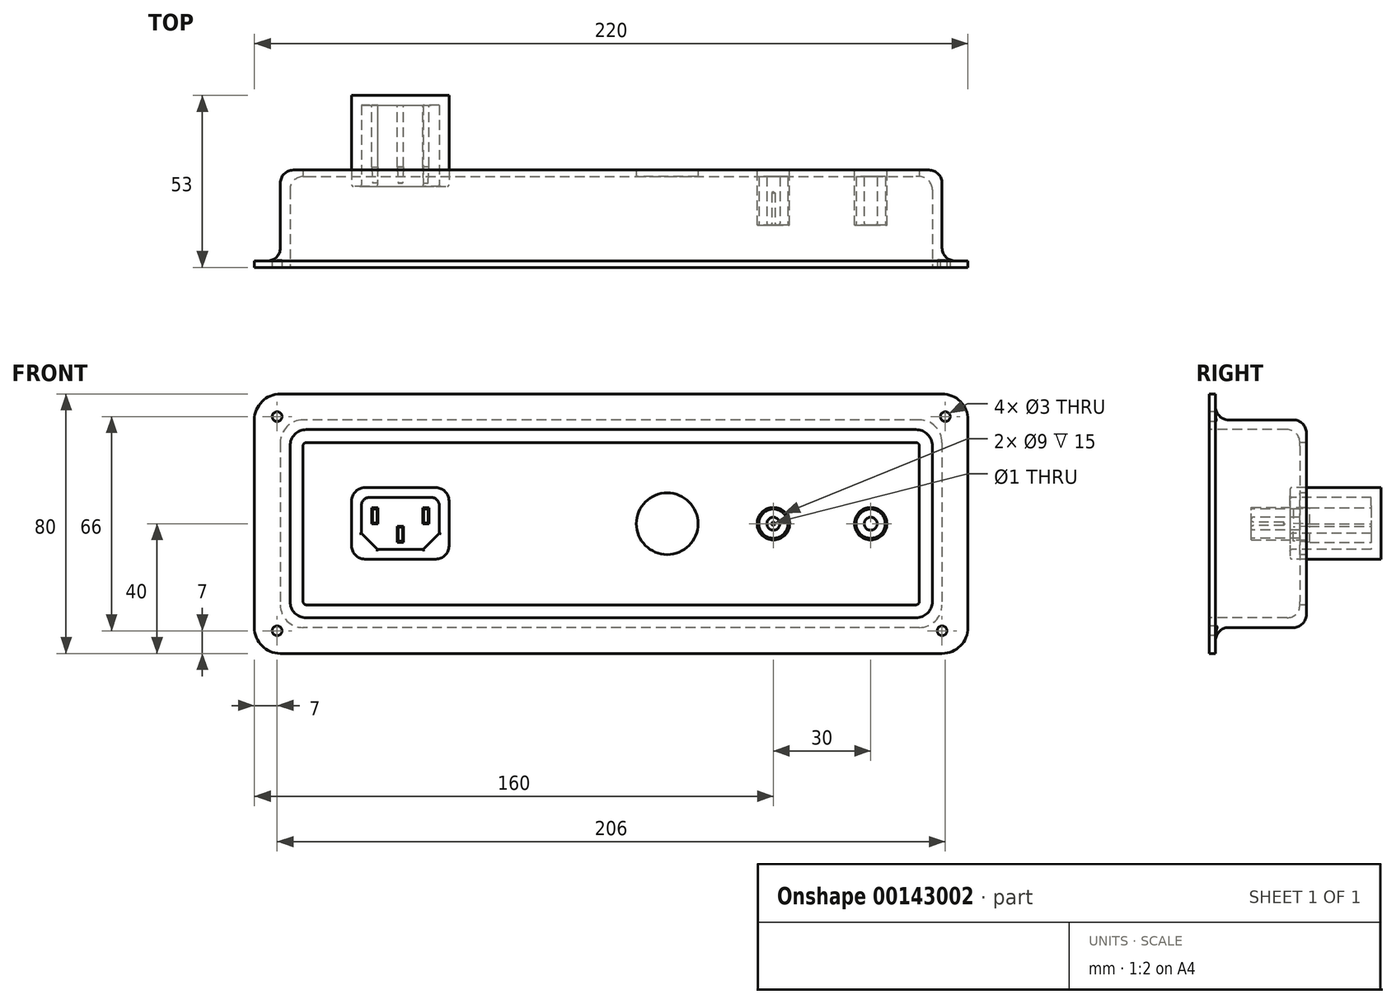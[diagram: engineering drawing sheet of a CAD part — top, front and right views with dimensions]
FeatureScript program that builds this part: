
annotation { "Feature Type Name" : "Feature", "Feature Type Description" : "" }
export const myFeature = defineFeature(function(context is Context, id is Id, definition is map)
    precondition{}
    {
        {
            var Q0;
            Q0=qCreatedBy(makeId("Front.planeOp"),FACE);
            var sketch = newSketch(context, id + "F0", { "sketchPlane" : qUnion([Q0])});
            skLineSegment(sketch, "E0.bottom", {"start": v(8, 0) * mm, "end": v(212, 0) * mm});
            skLineSegment(sketch, "E0.top", {"start": v(8, 80) * mm, "end": v(212, 80) * mm});
            skLineSegment(sketch, "E0.left", {"start": v(0, 8) * mm, "end": v(0, 72) * mm});
            skLineSegment(sketch, "E0.right", {"start": v(220, 8) * mm, "end": v(220, 72) * mm});
            skPoint(sketch, "E1.visualSharp", {"position": v(0, 80) * mm});
            skArc(sketch, "E1.filletArc", {"start": v(8, 80) * mm, "mid": v(2.34, 77.66) * mm, "end": v(0, 72) * mm});
            skPoint(sketch, "E2.visualSharp", {"position": v(220, 80) * mm});
            skArc(sketch, "E2.filletArc", {"start": v(220, 72) * mm, "mid": v(217.66, 77.66) * mm, "end": v(212, 80) * mm});
            skPoint(sketch, "E3.visualSharp", {"position": v(0, 0) * mm});
            skArc(sketch, "E3.filletArc", {"start": v(0, 8) * mm, "mid": v(2.34, 2.34) * mm, "end": v(8, 0) * mm});
            skPoint(sketch, "E4.visualSharp", {"position": v(220, 0) * mm});
            skArc(sketch, "E4.filletArc", {"start": v(212, 0) * mm, "mid": v(217.66, 2.34) * mm, "end": v(220, 8) * mm});
            skSolve(sketch);
        }
        {
            var Q0;
            Q0 = qSketchRegion(id + "F0", true);
            extrude(context, id + "F1", {"entities" : qUnion([Q0]), "depth" : 30 * mm});
        }
        {
            var Q0;
            Q0=makeQuery(id+"F1.opExtrude","CAP_FACE",FACE,{"disambiguationData":[OSD([sQuery(id+"F0.wireOp",EDGE,"E0.bottom"),sQuery(id+"F0.wireOp",EDGE,"E0.top"),sQuery(id+"F0.wireOp",EDGE,"E0.left"),sQuery(id+"F0.wireOp",EDGE,"E0.right"),sQuery(id+"F0.wireOp",EDGE,"E1.filletArc"),sQuery(id+"F0.wireOp",EDGE,"E2.filletArc"),sQuery(id+"F0.wireOp",EDGE,"E3.filletArc"),sQuery(id+"F0.wireOp",EDGE,"E4.filletArc")])],"isStart":true});
            var sketch = newSketch(context, id + "F2", { "sketchPlane" : qUnion([Q0])});
            skLineSegment(sketch, "E5.bottom", {"start": v(-205, 72) * mm, "end": v(-15, 72) * mm});
            skLineSegment(sketch, "E5.top", {"start": v(-205, 8) * mm, "end": v(-15, 8) * mm});
            skLineSegment(sketch, "E5.left", {"start": v(-212, 65) * mm, "end": v(-212, 15) * mm});
            skLineSegment(sketch, "E5.right", {"start": v(-8, 65) * mm, "end": v(-8, 15) * mm});
            skPoint(sketch, "E6.visualSharp", {"position": v(-212, 72) * mm});
            skArc(sketch, "E6.filletArc", {"start": v(-205, 72) * mm, "mid": v(-209.95, 69.95) * mm, "end": v(-212, 65) * mm});
            skPoint(sketch, "E7.visualSharp", {"position": v(-8, 72) * mm});
            skArc(sketch, "E7.filletArc", {"start": v(-8, 65) * mm, "mid": v(-10.05, 69.95) * mm, "end": v(-15, 72) * mm});
            skPoint(sketch, "E8.visualSharp", {"position": v(-8, 8) * mm});
            skArc(sketch, "E8.filletArc", {"start": v(-15, 8) * mm, "mid": v(-10.05, 10.05) * mm, "end": v(-8, 15) * mm});
            skPoint(sketch, "E9.visualSharp", {"position": v(-212, 8) * mm});
            skArc(sketch, "E9.filletArc", {"start": v(-212, 15) * mm, "mid": v(-209.95, 10.05) * mm, "end": v(-205, 8) * mm});
            skSolve(sketch);
        }
        {
            var Q0;
            Q0=makeQuery(id+"F2.imprint","IMPRINT",FACE,{"disambiguationData":[TD([[makeQuery(id+"F2.imprint","IMPRINT",EDGE,{"derivedFrom":sQuery(id+"F2.wireOp",EDGE,"E5.bottom")}),1.0]])]});
            extrude(context, id + "F3", {"entities" : qUnion([Q0]), "operationType" : NewBodyOperationType.REMOVE, "oppositeDirection" : true, "depth" : 28 * mm});
        }
        {
            var Q0;
            Q0=makeQuery(id+"F1.opExtrude","CAP_FACE",FACE,{"disambiguationData":[OSD([sQuery(id+"F0.wireOp",EDGE,"E0.bottom"),sQuery(id+"F0.wireOp",EDGE,"E0.top"),sQuery(id+"F0.wireOp",EDGE,"E0.left"),sQuery(id+"F0.wireOp",EDGE,"E0.right"),sQuery(id+"F0.wireOp",EDGE,"E1.filletArc"),sQuery(id+"F0.wireOp",EDGE,"E2.filletArc"),sQuery(id+"F0.wireOp",EDGE,"E3.filletArc"),sQuery(id+"F0.wireOp",EDGE,"E4.filletArc")])],"isStart":false});
            var sketch = newSketch(context, id + "F4", { "sketchPlane" : qUnion([Q0])});
            skPoint(sketch, "E10", {"position": v(11, 69) * mm});
            skPoint(sketch, "E11", {"position": v(209, 11) * mm});
            skLineSegment(sketch, "E12.bottom", {"start": v(16, 69) * mm, "end": v(204, 69) * mm});
            skLineSegment(sketch, "E12.top", {"start": v(16, 11) * mm, "end": v(204, 11) * mm});
            skLineSegment(sketch, "E12.left", {"start": v(11, 64) * mm, "end": v(11, 16) * mm});
            skLineSegment(sketch, "E12.right", {"start": v(209, 64) * mm, "end": v(209, 16) * mm});
            skArc(sketch, "E13.filletArc", {"start": v(16, 69) * mm, "mid": v(12.46, 67.54) * mm, "end": v(11, 64) * mm});
            skPoint(sketch, "E14.visualSharp", {"position": v(209, 69) * mm});
            skArc(sketch, "E14.filletArc", {"start": v(209, 64) * mm, "mid": v(207.54, 67.54) * mm, "end": v(204, 69) * mm});
            skArc(sketch, "E15.filletArc", {"start": v(204, 11) * mm, "mid": v(207.54, 12.46) * mm, "end": v(209, 16) * mm});
            skPoint(sketch, "E16.visualSharp", {"position": v(11, 11) * mm});
            skArc(sketch, "E16.filletArc", {"start": v(11, 16) * mm, "mid": v(12.46, 12.46) * mm, "end": v(16, 11) * mm});
            skSolve(sketch);
        }
        {
            var Q0;
            Q0=makeQuery(id+"F4.imprint","IMPRINT",FACE,{"disambiguationData":[TD([[makeQuery(id+"F4.imprint","IMPRINT",EDGE,{"derivedFrom":sQuery(id+"F4.wireOp",EDGE,"E12.bottom")}),-1.0]])]});
            extrude(context, id + "F5", {"entities" : qUnion([Q0]), "operationType" : NewBodyOperationType.REMOVE, "oppositeDirection" : true, "depth" : 28 * mm});
        }
        {
            var Q0;
            Q0=makeQuery(id+"F5.boolean.opBoolean","COPY",FACE,{"derivedFrom":makeQuery(id+"F5.opExtrude","CAP_FACE",FACE,{"disambiguationData":[OSD([sQuery(id+"F4.wireOp",EDGE,"E12.bottom"),sQuery(id+"F4.wireOp",EDGE,"E12.top"),sQuery(id+"F4.wireOp",EDGE,"E12.left"),sQuery(id+"F4.wireOp",EDGE,"E12.right"),sQuery(id+"F4.wireOp",EDGE,"E13.filletArc"),sQuery(id+"F4.wireOp",EDGE,"E14.filletArc"),sQuery(id+"F4.wireOp",EDGE,"E15.filletArc"),sQuery(id+"F4.wireOp",EDGE,"E16.filletArc")])],"isStart":false})});
            var Q1;
            Q1=makeQuery(id+"F1.opExtrude","CAP_FACE",FACE,{"disambiguationData":[OSD([sQuery(id+"F0.wireOp",EDGE,"E0.bottom"),sQuery(id+"F0.wireOp",EDGE,"E0.top"),sQuery(id+"F0.wireOp",EDGE,"E0.left"),sQuery(id+"F0.wireOp",EDGE,"E0.right"),sQuery(id+"F0.wireOp",EDGE,"E1.filletArc"),sQuery(id+"F0.wireOp",EDGE,"E2.filletArc"),sQuery(id+"F0.wireOp",EDGE,"E3.filletArc"),sQuery(id+"F0.wireOp",EDGE,"E4.filletArc")])],"isStart":true});
            var Q2;
            Q2=makeQuery(id+"F3.boolean.opBoolean","COPY",EDGE,{"derivedFrom":makeQuery(id+"F3.opExtrude","CAP_EDGE",EDGE,{"disambiguationData":[OSD([sQuery(id+"F2.wireOp",EDGE,"E5.top")])],"isStart":false})});
            var Q3;
            Q3=makeQuery(id+"F5.boolean.opBoolean","COPY",EDGE,{"derivedFrom":makeQuery(id+"F5.opExtrude","CAP_EDGE",EDGE,{"disambiguationData":[OSD([sQuery(id+"F4.wireOp",EDGE,"E12.left")])],"isStart":true})});
            fillet(context, id + "F6", {"entities" : qUnion([Q0, Q1, Q2, Q3]), "radius" : 4 * mm, "tangentPropagation" : true, "allowEdgeOverflow" : false});
        }
        {
            var Q0;
            Q0=makeQuery(id+"F1.opExtrude","CAP_FACE",FACE,{"disambiguationData":[OSD([sQuery(id+"F0.wireOp",EDGE,"E0.bottom"),sQuery(id+"F0.wireOp",EDGE,"E0.top"),sQuery(id+"F0.wireOp",EDGE,"E0.left"),sQuery(id+"F0.wireOp",EDGE,"E0.right"),sQuery(id+"F0.wireOp",EDGE,"E1.filletArc"),sQuery(id+"F0.wireOp",EDGE,"E2.filletArc"),sQuery(id+"F0.wireOp",EDGE,"E3.filletArc"),sQuery(id+"F0.wireOp",EDGE,"E4.filletArc")])],"isStart":false});
            var sketch = newSketch(context, id + "F7", { "sketchPlane" : qUnion([Q0])});
            skPoint(sketch, "E17", {"position": v(213, 73) * mm});
            skPoint(sketch, "E18", {"position": v(7, 73) * mm});
            skPoint(sketch, "E19", {"position": v(212, 7) * mm});
            skPoint(sketch, "E20", {"position": v(7, 7) * mm});
            skSolve(sketch);
        }
        {
            var Q0;
            Q0=sQuery(id+"F7.wireOp",VERTEX,"E18");
            var Q1;
            Q1=sQuery(id+"F7.wireOp",VERTEX,"E17");
            var Q2;
            Q2=sQuery(id+"F7.wireOp",VERTEX,"E19");
            var Q3;
            Q3=sQuery(id+"F7.wireOp",VERTEX,"E20");
            var Q4;
            Q4=makeQuery(id+"F1.opExtrude","SWEPT_BODY",BODY,{"disambiguationData":[OSD([sQuery(id+"F0.wireOp",EDGE,"E0.bottom"),sQuery(id+"F0.wireOp",EDGE,"E0.top"),sQuery(id+"F0.wireOp",EDGE,"E0.left"),sQuery(id+"F0.wireOp",EDGE,"E0.right"),sQuery(id+"F0.wireOp",EDGE,"E1.filletArc"),sQuery(id+"F0.wireOp",EDGE,"E2.filletArc"),sQuery(id+"F0.wireOp",EDGE,"E3.filletArc"),sQuery(id+"F0.wireOp",EDGE,"E4.filletArc")])]});
            hole(context, id + "F8", {"style" : HoleStyle.SIMPLE, "endStyle" : HoleEndStyle.THROUGH, "holeDiameter" : 3 * mm, "locations" : qUnion([Q0, Q1, Q2, Q3]), "scope" : qUnion([Q4]), "isTappedThrough" : true});
        }
        {
            var Q0;
            Q0=makeQuery(id+"F5.boolean.opBoolean","COPY",FACE,{"derivedFrom":makeQuery(id+"F5.opExtrude","CAP_FACE",FACE,{"disambiguationData":[OSD([sQuery(id+"F4.wireOp",EDGE,"E12.bottom"),sQuery(id+"F4.wireOp",EDGE,"E12.top"),sQuery(id+"F4.wireOp",EDGE,"E12.left"),sQuery(id+"F4.wireOp",EDGE,"E12.right"),sQuery(id+"F4.wireOp",EDGE,"E13.filletArc"),sQuery(id+"F4.wireOp",EDGE,"E14.filletArc"),sQuery(id+"F4.wireOp",EDGE,"E15.filletArc"),sQuery(id+"F4.wireOp",EDGE,"E16.filletArc")])],"isStart":false})});
            var sketch = newSketch(context, id + "F9", { "sketchPlane" : qUnion([Q0])});
            skLineSegment(sketch, "E21", {"start": v(16, 40) * mm, "end": v(205, 40) * mm, "construction": true});
            skPoint(sketch, "E21.startSnap0", {"position": v(15, 40) * mm});
            skPoint(sketch, "E22", {"position": v(190, 40) * mm});
            skPoint(sketch, "E23", {"position": v(160, 40) * mm});
            skLineSegment(sketch, "E24", {"start": v(160, 40) * mm, "end": v(190, 40) * mm, "construction": true});
            skLineSegment(sketch, "E25", {"start": v(175, 40) * mm, "end": v(175, 58.9) * mm, "construction": true});
            skLineSegment(sketch, "E26", {"start": v(175, 58.9) * mm, "end": v(175, 21.63) * mm, "construction": true});
            skCircle(sketch, "E27", {"center": v(160, 40) * mm, "radius": 5 * mm});
            skCircle(sketch, "E28.MirrorC", {"center": v(190, 40) * mm, "radius": 5 * mm});
            skSolve(sketch);
        }
        {
            var Q0;
            Q0 = qSketchRegion(id + "F9", true);
            extrude(context, id + "F10", {"entities" : qUnion([Q0]), "operationType" : NewBodyOperationType.ADD, "depth" : 15 * mm, "offsetDistance" : 25 * mm});
        }
        {
            var Q0;
            Q0=makeQuery(id+"F10.opExtrude","CAP_FACE",FACE,{"disambiguationData":[OSD([sQuery(id+"F9.wireOp",EDGE,"E27")])],"isStart":false});
            var sketch = newSketch(context, id + "F11", { "sketchPlane" : qUnion([Q0])});
            skCircle(sketch, "E29", {"center": v(160, 40) * mm, "radius": 4.5 * mm});
            skCircle(sketch, "E30", {"center": v(160, 40) * mm, "radius": 2 * mm});
            skCircle(sketch, "E31.MirrorC", {"center": v(190, 40) * mm, "radius": 4.5 * mm});
            skCircle(sketch, "E32.MirrorC", {"center": v(190, 40) * mm, "radius": 2 * mm});
            skSolve(sketch);
        }
        {
            var Q0;
            Q0 = qSketchRegion(id + "F11", true);
            extrude(context, id + "F12", {"entities" : qUnion([Q0]), "operationType" : NewBodyOperationType.REMOVE, "oppositeDirection" : true, "depth" : 15 * mm});
        }
        {
            var Q0;
            Q0=makeQuery(id+"F12.boolean.opBoolean","SPLIT",FACE,{"disambiguationData":[TD([makeQuery(id+"F12.opExtrude","SWEPT_FACE",FACE,{"disambiguationData":[OSD([sQuery(id+"F11.wireOp",EDGE,"E30")])]})])],"derivedFrom":makeQuery(id+"F10.opExtrude","CAP_FACE",FACE,{"disambiguationData":[OSD([sQuery(id+"F9.wireOp",EDGE,"E27")])],"isStart":false})});
            var sketch = newSketch(context, id + "F13", { "sketchPlane" : qUnion([Q0])});
            skPoint(sketch, "E33", {"position": v(160, 40) * mm});
            skCircle(sketch, "E34", {"center": v(160, 40) * mm, "radius": 0.5 * mm});
            skCircle(sketch, "E35.MirrorC", {"center": v(190, 40) * mm, "radius": 0.5 * mm});
            skSolve(sketch);
        }
        {
            var Q0;
            Q0=sQuery(id+"F13.wireOp",VERTEX,"E34.center");
            var Q1;
            Q1=sQuery(id+"F13.wireOp",VERTEX,"E35.MirrorC.center");
            var Q2;
            Q2=makeQuery(id+"F1.opExtrude","SWEPT_BODY",BODY,{"disambiguationData":[OSD([sQuery(id+"F0.wireOp",EDGE,"E0.bottom"),sQuery(id+"F0.wireOp",EDGE,"E0.top"),sQuery(id+"F0.wireOp",EDGE,"E0.left"),sQuery(id+"F0.wireOp",EDGE,"E0.right"),sQuery(id+"F0.wireOp",EDGE,"E1.filletArc"),sQuery(id+"F0.wireOp",EDGE,"E2.filletArc"),sQuery(id+"F0.wireOp",EDGE,"E3.filletArc"),sQuery(id+"F0.wireOp",EDGE,"E4.filletArc")])]});
            hole(context, id + "F14", {"style" : HoleStyle.SIMPLE, "endStyle" : HoleEndStyle.BLIND, "holeDiameter" : 1 * mm, "holeDepth" : 10 * mm, "locations" : qUnion([Q0, Q1]), "scope" : qUnion([Q2])});
        }
        {
            var Q0;
            Q0=makeQuery(id+"F12.boolean.opBoolean","SPLIT",FACE,{"disambiguationData":[TD([makeQuery(id+"F12.opExtrude","SWEPT_FACE",FACE,{"disambiguationData":[OSD([sQuery(id+"F11.wireOp",EDGE,"E30")])]})])],"derivedFrom":makeQuery(id+"F10.opExtrude","CAP_FACE",FACE,{"disambiguationData":[OSD([sQuery(id+"F9.wireOp",EDGE,"E27")])],"isStart":false})});
            var Q1;
            Q1=makeQuery(id+"F12.boolean.opBoolean","SPLIT",FACE,{"disambiguationData":[TD([makeQuery(id+"F12.opExtrude","SWEPT_FACE",FACE,{"disambiguationData":[OSD([sQuery(id+"F11.wireOp",EDGE,"E32.MirrorC")])]})])],"derivedFrom":makeQuery(id+"F10.opExtrude","CAP_FACE",FACE,{"disambiguationData":[OSD([sQuery(id+"F9.wireOp",EDGE,"E28.MirrorC")])],"isStart":false})});
            fillet(context, id + "F15", {"entities" : qUnion([Q0, Q1]), "radius" : 0.7 * mm, "tangentPropagation" : true, "allowEdgeOverflow" : false});
        }
        {
            var Q0;
            Q0=makeQuery(id+"F9.imprint","IMPRINT",FACE,{"disambiguationData":[TD([[makeQuery(id+"F9.imprint","IMPRINT",EDGE,{"derivedFrom":sQuery(id+"F9.wireOp",EDGE,"E27")}),-1.0]])]});
            var sketch = newSketch(context, id + "F16", { "sketchPlane" : qUnion([Q0])});
            skLineSegment(sketch, "E36.bottom", {"start": v(34, 51.1) * mm, "end": v(56, 51.1) * mm});
            skLineSegment(sketch, "E36.top", {"start": v(34, 29.1) * mm, "end": v(56, 29.1) * mm});
            skLineSegment(sketch, "E36.left", {"start": v(30, 47.1) * mm, "end": v(30, 33.1) * mm});
            skLineSegment(sketch, "E36.right", {"start": v(60, 47.1) * mm, "end": v(60, 33.1) * mm});
            skPoint(sketch, "E37.visualSharp", {"position": v(30, 51.1) * mm});
            skArc(sketch, "E37.filletArc", {"start": v(34, 51.1) * mm, "mid": v(31.17, 49.93) * mm, "end": v(30, 47.1) * mm});
            skPoint(sketch, "E38.visualSharp", {"position": v(60, 51.1) * mm});
            skArc(sketch, "E38.filletArc", {"start": v(60, 47.1) * mm, "mid": v(58.83, 49.93) * mm, "end": v(56, 51.1) * mm});
            skPoint(sketch, "E39.visualSharp", {"position": v(60, 29.1) * mm});
            skArc(sketch, "E39.filletArc", {"start": v(56, 29.1) * mm, "mid": v(58.83, 30.27) * mm, "end": v(60, 33.1) * mm});
            skPoint(sketch, "E40.visualSharp", {"position": v(30, 29.1) * mm});
            skArc(sketch, "E40.filletArc", {"start": v(30, 33.1) * mm, "mid": v(31.17, 30.27) * mm, "end": v(34, 29.1) * mm});
            skSolve(sketch);
        }
        {
            var Q0;
            Q0 = qSketchRegion(id + "F16", true);
            extrude(context, id + "F17", {"entities" : qUnion([Q0]), "operationType" : NewBodyOperationType.ADD, "depth" : 3 * mm, "hasSecondDirection" : true, "secondDirectionOppositeDirection" : true, "secondDirectionDepth" : 25 * mm});
        }
        {
            var Q0;
            Q0=makeQuery(id+"F17.opExtrude","CAP_FACE",FACE,{"disambiguationData":[OSD([sQuery(id+"F16.wireOp",EDGE,"E36.bottom"),sQuery(id+"F16.wireOp",EDGE,"E36.top"),sQuery(id+"F16.wireOp",EDGE,"E36.left"),sQuery(id+"F16.wireOp",EDGE,"E36.right"),sQuery(id+"F16.wireOp",EDGE,"E37.filletArc"),sQuery(id+"F16.wireOp",EDGE,"E38.filletArc"),sQuery(id+"F16.wireOp",EDGE,"E39.filletArc"),sQuery(id+"F16.wireOp",EDGE,"E40.filletArc")])],"isStart":false});
            var sketch = newSketch(context, id + "F18", { "sketchPlane" : qUnion([Q0])});
            skLineSegment(sketch, "E41", {"start": v(35.5, 48.1) * mm, "end": v(54.5, 48.1) * mm});
            skLineSegment(sketch, "E42", {"start": v(57, 45.6) * mm, "end": v(57, 37.1) * mm});
            skLineSegment(sketch, "E43", {"start": v(33, 45.6) * mm, "end": v(33, 37.1) * mm});
            skLineSegment(sketch, "E44", {"start": v(33.07, 32.1) * mm, "end": v(75.83, 32.1) * mm, "construction": true});
            skLineSegment(sketch, "E45", {"start": v(57, 37.1) * mm, "end": v(52, 32.1) * mm});
            skLineSegment(sketch, "E46", {"start": v(33, 37.1) * mm, "end": v(38, 32.1) * mm});
            skLineSegment(sketch, "E47", {"start": v(38, 32.1) * mm, "end": v(52, 32.1) * mm});
            skPoint(sketch, "E48.visualSharp", {"position": v(33, 48.1) * mm});
            skArc(sketch, "E48.filletArc", {"start": v(35.5, 48.1) * mm, "mid": v(33.73, 47.37) * mm, "end": v(33, 45.6) * mm});
            skPoint(sketch, "E49.visualSharp", {"position": v(57, 48.1) * mm});
            skArc(sketch, "E49.filletArc", {"start": v(57, 45.6) * mm, "mid": v(56.27, 47.37) * mm, "end": v(54.5, 48.1) * mm});
            skSolve(sketch);
        }
        {
            var Q0;
            {var subQ0=sQuery(id+"F18.wireOp",EDGE,"E42");Q0=makeQuery(id+"F18.imprint","IMPRINT",FACE,{"disambiguationData":[TD([[makeQuery(id+"F18.imprint","IMPRINT",EDGE,{"derivedFrom":subQ0}),-1.0]])]});}
            extrude(context, id + "F19", {"entities" : qUnion([Q0]), "operationType" : NewBodyOperationType.REMOVE, "oppositeDirection" : true, "depth" : 25 * mm});
        }
        {
            var Q0;
            Q0=makeQuery(id+"F19.boolean.opBoolean","COPY",FACE,{"derivedFrom":makeQuery(id+"F19.opExtrude","CAP_FACE",FACE,{"disambiguationData":[OSD([sQuery(id+"F18.wireOp",EDGE,"E41"),sQuery(id+"F18.wireOp",EDGE,"E42"),sQuery(id+"F18.wireOp",EDGE,"EqLcRgzD-fBd3-cg1o-OcqL-YxDi5VAXH1On"),sQuery(id+"F18.wireOp",EDGE,"owGIvLdP-Utom-xGj5-LzAy-hpVVH1rjGkJn"),sQuery(id+"F18.wireOp",EDGE,"867b260c-1252-4fc6-b47a-d03f289bcd2f.filletArc"),sQuery(id+"F18.wireOp",EDGE,"E43"),sQuery(id+"F18.wireOp",EDGE,"edTf08Cn-y1Es-Mu3l-SgCF-yclIuyavZhc0"),sQuery(id+"F18.wireOp",EDGE,"dac244f5-5067-4b4c-9d92-0b75d97c7b22.filletArc"),sQuery(id+"F18.wireOp",EDGE,"11a2030b-5c4c-4d8f-9b6e-7c2cbcffeb91.filletArc"),sQuery(id+"F18.wireOp",EDGE,"927fffb7-791c-4cfc-804e-2c8d71075ebf.filletArc"),sQuery(id+"F18.wireOp",EDGE,"01267c1d-3c43-40b3-8e76-5d94c63c29d4.filletArc"),sQuery(id+"F18.wireOp",EDGE,"ba731b8e-ff5e-4bcd-9941-3f4ddfb2e2d0.filletArc")])],"isStart":false})});
            var sketch = newSketch(context, id + "F20", { "sketchPlane" : qUnion([Q0])});
            skLineSegment(sketch, "E50.bottom", {"start": v(51.88, 44.91) * mm, "end": v(53.88, 44.91) * mm});
            skLineSegment(sketch, "E50.top", {"start": v(51.88, 39.91) * mm, "end": v(53.88, 39.91) * mm});
            skLineSegment(sketch, "E50.left", {"start": v(51.88, 44.91) * mm, "end": v(51.88, 39.91) * mm});
            skLineSegment(sketch, "E50.right", {"start": v(53.88, 44.91) * mm, "end": v(53.88, 39.91) * mm});
            skLineSegment(sketch, "E51", {"start": v(45, 48.1) * mm, "end": v(45, 26.06) * mm, "construction": true});
            skLineSegment(sketch, "E52.left", {"start": v(45, 39.28) * mm, "end": v(45, 39.28) * mm});
            skLineSegment(sketch, "E52.right", {"start": v(44, 39.26) * mm, "end": v(44, 34.26) * mm});
            skLineSegment(sketch, "E53.MirrorCS", {"start": v(38.12, 39.91) * mm, "end": v(36.12, 39.91) * mm});
            skLineSegment(sketch, "E54.MirrorCS", {"start": v(38.12, 44.91) * mm, "end": v(38.12, 39.91) * mm});
            skLineSegment(sketch, "E55.MirrorCS", {"start": v(38.12, 44.91) * mm, "end": v(36.12, 44.91) * mm});
            skLineSegment(sketch, "E56.MirrorCS", {"start": v(36.12, 44.91) * mm, "end": v(36.12, 39.91) * mm});
            skLineSegment(sketch, "E57", {"start": v(44, 34.26) * mm, "end": v(45, 34.26) * mm, "construction": true});
            skLineSegment(sketch, "E58.MirrorCS", {"start": v(46, 34.26) * mm, "end": v(45, 34.26) * mm, "construction": true});
            skLineSegment(sketch, "E59.MirrorCS", {"start": v(46, 39.26) * mm, "end": v(46, 34.26) * mm});
            skLineSegment(sketch, "E60", {"start": v(44, 39.26) * mm, "end": v(46, 39.26) * mm});
            skLineSegment(sketch, "E61", {"start": v(44, 34.26) * mm, "end": v(46, 34.26) * mm});
            skSolve(sketch);
        }
        {
            var Q0;
            Q0 = qSketchRegion(id + "F20", true);
            extrude(context, id + "F21", {"entities" : qUnion([Q0]), "operationType" : NewBodyOperationType.ADD, "depth" : 24 * mm});
        }
        {
            var Q0;
            Q0=makeQuery(id+"F21.opExtrude","CAP_FACE",FACE,{"disambiguationData":[OSD([sQuery(id+"F20.wireOp",EDGE,"E50.bottom"),sQuery(id+"F20.wireOp",EDGE,"E50.top"),sQuery(id+"F20.wireOp",EDGE,"E50.left"),sQuery(id+"F20.wireOp",EDGE,"E50.right")])],"isStart":false});
            chamfer(context, id + "F22", {"entities" : qUnion([Q0]), "chamferType" : ChamferType.OFFSET_ANGLE, "width" : 5 * mm, "oppositeDirection" : false, "angle" : 4 * degree});
        }
        {
            var Q0;
            Q0=makeQuery(id+"F21.opExtrude","CAP_FACE",FACE,{"disambiguationData":[OSD([sQuery(id+"F20.wireOp",EDGE,"E52.right"),sQuery(id+"F20.wireOp",EDGE,"E59.MirrorCS"),sQuery(id+"F20.wireOp",EDGE,"E60"),sQuery(id+"F20.wireOp",EDGE,"E61")])],"isStart":false});
            chamfer(context, id + "F23", {"entities" : qUnion([Q0]), "chamferType" : ChamferType.OFFSET_ANGLE, "width" : 5 * mm, "oppositeDirection" : true, "angle" : 4 * degree});
        }
        {
            var Q0;
            Q0=makeQuery(id+"F21.opExtrude","CAP_FACE",FACE,{"disambiguationData":[OSD([sQuery(id+"F20.wireOp",EDGE,"E53.MirrorCS"),sQuery(id+"F20.wireOp",EDGE,"E54.MirrorCS"),sQuery(id+"F20.wireOp",EDGE,"E55.MirrorCS"),sQuery(id+"F20.wireOp",EDGE,"E56.MirrorCS")])],"isStart":false});
            chamfer(context, id + "F24", {"entities" : qUnion([Q0]), "chamferType" : ChamferType.OFFSET_ANGLE, "width" : 5 * mm, "oppositeDirection" : false, "angle" : 4 * degree, "tangentPropagation" : true});
        }
        {
            var Q0;
            Q0=makeQuery(id+"F17.opExtrude","CAP_FACE",FACE,{"disambiguationData":[OSD([sQuery(id+"F16.wireOp",EDGE,"E36.bottom"),sQuery(id+"F16.wireOp",EDGE,"E36.top"),sQuery(id+"F16.wireOp",EDGE,"E36.left"),sQuery(id+"F16.wireOp",EDGE,"E36.right"),sQuery(id+"F16.wireOp",EDGE,"E37.filletArc"),sQuery(id+"F16.wireOp",EDGE,"E38.filletArc"),sQuery(id+"F16.wireOp",EDGE,"E39.filletArc"),sQuery(id+"F16.wireOp",EDGE,"E40.filletArc")])],"isStart":false});
            fillet(context, id + "F25", {"entities" : qUnion([Q0]), "radius" : 0.5 * mm, "tangentPropagation" : true, "allowEdgeOverflow" : false});
        }
        {
            var Q0;
            {var subQ0=sQuery(id+"F4.wireOp",EDGE,"E12.left");var subQ1=sQuery(id+"F4.wireOp",EDGE,"E16.filletArc");var subQ2=sQuery(id+"F4.wireOp",EDGE,"E15.filletArc");var subQ3=sQuery(id+"F4.wireOp",EDGE,"E14.filletArc");var subQ4=sQuery(id+"F4.wireOp",EDGE,"E13.filletArc");var subQ5=sQuery(id+"F4.wireOp",EDGE,"E12.bottom");var subQ6=sQuery(id+"F4.wireOp",EDGE,"E12.top");var subQ7=sQuery(id+"F4.wireOp",EDGE,"E12.right");Q0=makeQuery(id+"F10.boolean.opBoolean","SPLIT",FACE,{"disambiguationData":[TD([makeQuery(id+"F10.opExtrude","SWEPT_FACE",FACE,{"disambiguationData":[OSD([sQuery(id+"F9.wireOp",EDGE,"E27")])]})])],"derivedFrom":makeQuery(id+"F5.boolean.opBoolean","COPY",FACE,{"derivedFrom":makeQuery(id+"F5.opExtrude","CAP_FACE",FACE,{"disambiguationData":[OSD([subQ5,subQ6,subQ0,subQ7,subQ4,subQ3,subQ2,subQ1])],"isStart":false})})});}
            var sketch = newSketch(context, id + "F26", { "sketchPlane" : qUnion([Q0])});
            skLineSegment(sketch, "E62", {"start": v(15, 40) * mm, "end": v(205, 40) * mm, "construction": true});
            skPoint(sketch, "E63", {"position": v(107.27, 40) * mm});
            skLineSegment(sketch, "E64", {"start": v(107.27, 64.07) * mm, "end": v(107.27, 19.02) * mm, "construction": true});
            skPoint(sketch, "E65", {"position": v(87.27, 40) * mm});
            skCircle(sketch, "E66", {"center": v(87.27, 40) * mm, "radius": 9.5 * mm});
            skCircle(sketch, "E67.MirrorC", {"center": v(127.27, 40) * mm, "radius": 9.5 * mm});
            skSolve(sketch);
        }
        {
            var Q0;
            Q0=makeQuery(id+"F26.imprint","IMPRINT",FACE,{"disambiguationData":[TD([[makeQuery(id+"F26.imprint","IMPRINT",EDGE,{"derivedFrom":sQuery(id+"F26.wireOp",EDGE,"E66")}),1.0]])]});
            var Q1;
            Q1=makeQuery(id+"F26.imprint","IMPRINT",FACE,{"disambiguationData":[TD([[makeQuery(id+"F26.imprint","IMPRINT",EDGE,{"derivedFrom":sQuery(id+"F26.wireOp",EDGE,"E67.MirrorC")}),-1.0]])]});
            var Q2;
            Q2=sQuery(id+"F26.wireOp",EDGE,"E66");
            var Q3;
            Q3=sQuery(id+"F26.wireOp",EDGE,"E67.MirrorC");
            extrude(context, id + "F27", {"entities" : qUnion([Q0, Q1]), "operationType" : NewBodyOperationType.REMOVE, "surfaceEntities" : qUnion([Q2, Q3]), "endBound" : BoundingType.UP_TO_NEXT, "oppositeDirection" : true, "depth" : 25 * mm, "offsetDistance" : 25 * mm});
        }
    });
